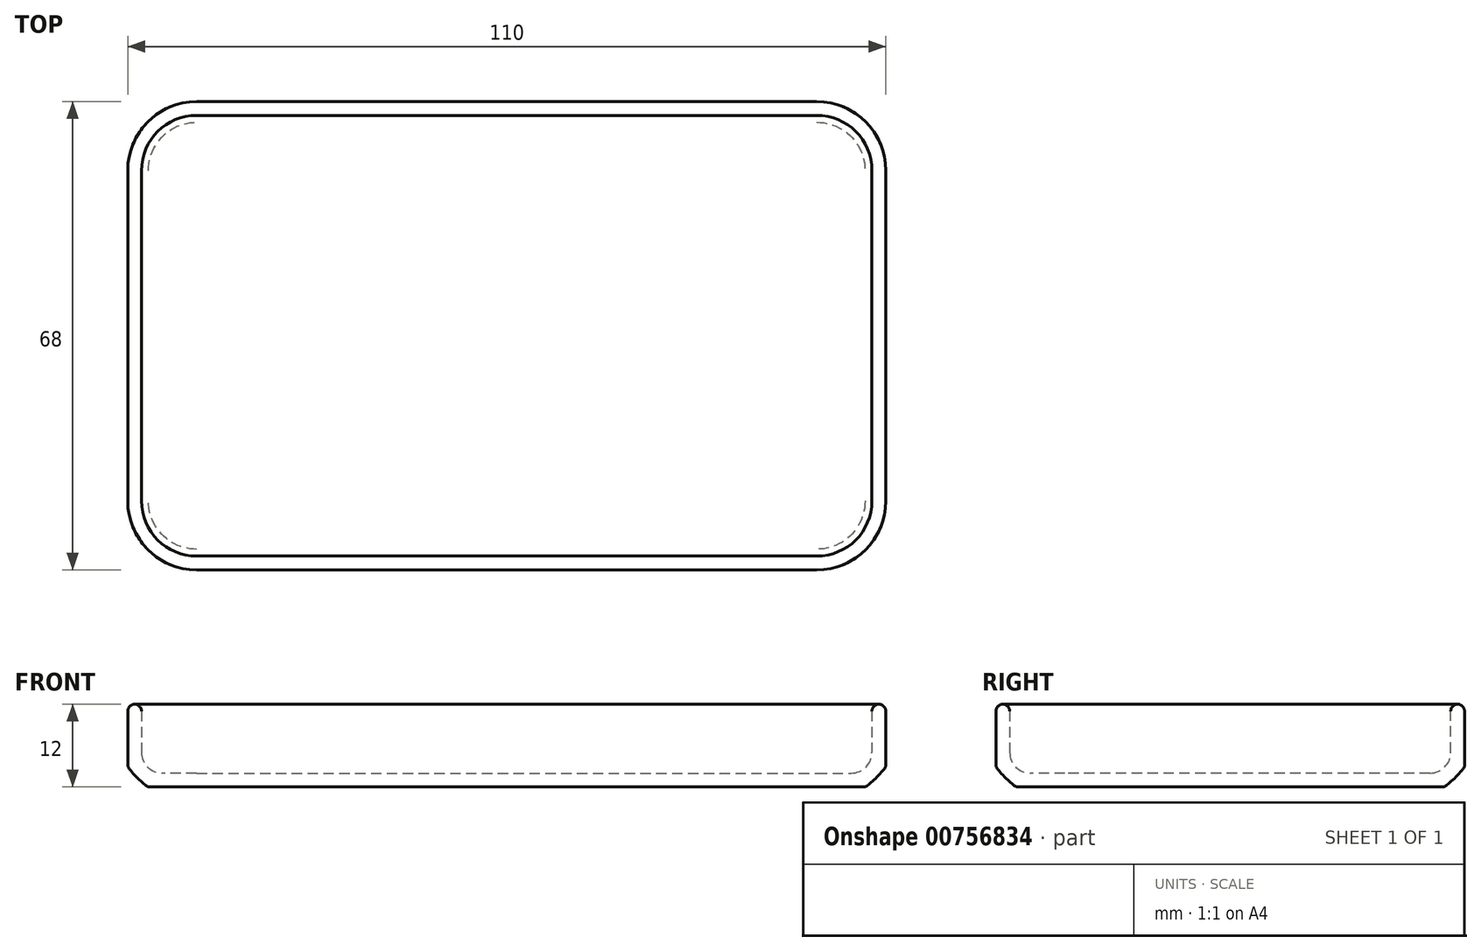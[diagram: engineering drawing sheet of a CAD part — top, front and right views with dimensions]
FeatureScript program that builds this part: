
annotation { "Feature Type Name" : "Feature", "Feature Type Description" : "" }
export const myFeature = defineFeature(function(context is Context, id is Id, definition is map)
    precondition{}
    {
        {
            var Q0;
            Q0=qCreatedBy(makeId("Top.planeOp"),FACE);
            var sketch = newSketch(context, id + "F0", { "sketchPlane" : qUnion([Q0])});
            skLineSegment(sketch, "E0", {"start": v(0, 34) * mm, "end": v(-45, 34) * mm});
            skLineSegment(sketch, "E1", {"start": v(-55, 24) * mm, "end": v(-55, 0) * mm});
            skPoint(sketch, "E2.visualSharp", {"position": v(-55, 34) * mm});
            skArc(sketch, "E2.filletArc", {"start": v(-45, 34) * mm, "mid": v(-52.07, 31.07) * mm, "end": v(-55, 24) * mm});
            skLineSegment(sketch, "E3.MirrorCS", {"start": v(0, 34) * mm, "end": v(45, 34) * mm});
            skLineSegment(sketch, "E4.MirrorCS", {"start": v(55, 24) * mm, "end": v(55, 0) * mm});
            skPoint(sketch, "E5.MirrorP", {"position": v(55, 34) * mm});
            skArc(sketch, "E6.MirrorCS", {"start": v(45, 34) * mm, "mid": v(52.07, 31.07) * mm, "end": v(55, 24) * mm});
            skLineSegment(sketch, "E7.MirrorCS", {"start": v(55, -24) * mm, "end": v(55, 0) * mm});
            skLineSegment(sketch, "E8.MirrorCS", {"start": v(-55, -24) * mm, "end": v(-55, 0) * mm});
            skLineSegment(sketch, "E9.MirrorCS", {"start": v(0, -34) * mm, "end": v(-45, -34) * mm});
            skLineSegment(sketch, "E10.MirrorCS", {"start": v(0, -34) * mm, "end": v(45, -34) * mm});
            skPoint(sketch, "E11.MirrorP", {"position": v(-55, -34) * mm});
            skPoint(sketch, "E12.MirrorP", {"position": v(55, -34) * mm});
            skArc(sketch, "E13.MirrorCS", {"start": v(45, -34) * mm, "mid": v(52.07, -31.07) * mm, "end": v(55, -24) * mm});
            skArc(sketch, "E14.MirrorCS", {"start": v(-45, -34) * mm, "mid": v(-52.07, -31.07) * mm, "end": v(-55, -24) * mm});
            skSolve(sketch);
        }
        {
            var Q0;
            Q0 = qSketchRegion(id + "F0", true);
            extrude(context, id + "F1", {"entities" : qUnion([Q0]), "depth" : 12 * mm, "offsetDistance" : 25 * mm});
        }
        {
            var Q0;
            Q0=makeQuery(id+"F1.opExtrude","CAP_FACE",FACE,{"disambiguationData":[OSD([sQuery(id+"F0.wireOp",EDGE,"E1"),sQuery(id+"F0.wireOp",EDGE,"E0"),sQuery(id+"F0.wireOp",EDGE,"E2.filletArc"),sQuery(id+"F0.wireOp",EDGE,"E4.MirrorCS"),sQuery(id+"F0.wireOp",EDGE,"E3.MirrorCS"),sQuery(id+"F0.wireOp",EDGE,"E6.MirrorCS"),sQuery(id+"F0.wireOp",EDGE,"E10.MirrorCS"),sQuery(id+"F0.wireOp",EDGE,"E13.MirrorCS"),sQuery(id+"F0.wireOp",EDGE,"E7.MirrorCS"),sQuery(id+"F0.wireOp",EDGE,"E8.MirrorCS"),sQuery(id+"F0.wireOp",EDGE,"E9.MirrorCS"),sQuery(id+"F0.wireOp",EDGE,"E14.MirrorCS")])],"isStart":false});
            shell(context, id + "F2", {"entities" : qUnion([Q0]), "thickness" : 2 * mm});
        }
        {
            var Q0;
            Q0=makeQuery(id+"F2.opShell","OFFSET_FACE",FACE,{"disambiguationData":[OSD([sQuery(id+"F0.wireOp",EDGE,"E1"),sQuery(id+"F0.wireOp",EDGE,"E0"),sQuery(id+"F0.wireOp",EDGE,"E2.filletArc"),sQuery(id+"F0.wireOp",EDGE,"E4.MirrorCS"),sQuery(id+"F0.wireOp",EDGE,"E3.MirrorCS"),sQuery(id+"F0.wireOp",EDGE,"E6.MirrorCS"),sQuery(id+"F0.wireOp",EDGE,"E10.MirrorCS"),sQuery(id+"F0.wireOp",EDGE,"E13.MirrorCS"),sQuery(id+"F0.wireOp",EDGE,"E7.MirrorCS"),sQuery(id+"F0.wireOp",EDGE,"E8.MirrorCS"),sQuery(id+"F0.wireOp",EDGE,"E9.MirrorCS"),sQuery(id+"F0.wireOp",EDGE,"E14.MirrorCS")])]});
            fillet(context, id + "F3", {"entities" : qUnion([Q0]), "radius" : 3 * mm, "tangentPropagation" : true, "allowEdgeOverflow" : false});
        }
        {
            var Q0;
            Q0=makeQuery(id+"F1.opExtrude","CAP_FACE",FACE,{"disambiguationData":[OSD([sQuery(id+"F0.wireOp",EDGE,"E1"),sQuery(id+"F0.wireOp",EDGE,"E0"),sQuery(id+"F0.wireOp",EDGE,"E2.filletArc"),sQuery(id+"F0.wireOp",EDGE,"E4.MirrorCS"),sQuery(id+"F0.wireOp",EDGE,"E3.MirrorCS"),sQuery(id+"F0.wireOp",EDGE,"E6.MirrorCS"),sQuery(id+"F0.wireOp",EDGE,"E10.MirrorCS"),sQuery(id+"F0.wireOp",EDGE,"E13.MirrorCS"),sQuery(id+"F0.wireOp",EDGE,"E7.MirrorCS"),sQuery(id+"F0.wireOp",EDGE,"E8.MirrorCS"),sQuery(id+"F0.wireOp",EDGE,"E9.MirrorCS"),sQuery(id+"F0.wireOp",EDGE,"E14.MirrorCS")])],"isStart":false});
            fillet(context, id + "F4", {"entities" : qUnion([Q0]), "radius" : 1 * mm, "tangentPropagation" : true, "allowEdgeOverflow" : false});
        }
        {
            var Q0;
            Q0=makeQuery(id+"F1.opExtrude","CAP_FACE",FACE,{"disambiguationData":[OSD([sQuery(id+"F0.wireOp",EDGE,"E1"),sQuery(id+"F0.wireOp",EDGE,"E0"),sQuery(id+"F0.wireOp",EDGE,"E2.filletArc"),sQuery(id+"F0.wireOp",EDGE,"E4.MirrorCS"),sQuery(id+"F0.wireOp",EDGE,"E3.MirrorCS"),sQuery(id+"F0.wireOp",EDGE,"E6.MirrorCS"),sQuery(id+"F0.wireOp",EDGE,"E10.MirrorCS"),sQuery(id+"F0.wireOp",EDGE,"E13.MirrorCS"),sQuery(id+"F0.wireOp",EDGE,"E7.MirrorCS"),sQuery(id+"F0.wireOp",EDGE,"E8.MirrorCS"),sQuery(id+"F0.wireOp",EDGE,"E9.MirrorCS"),sQuery(id+"F0.wireOp",EDGE,"E14.MirrorCS")])],"isStart":true});
            fillet(context, id + "F5", {"entities" : qUnion([Q0]), "radius" : 3 * mm, "rho" : 0.1, "crossSection" : FilletCrossSection.CONIC, "allowEdgeOverflow" : false});
        }
    });
